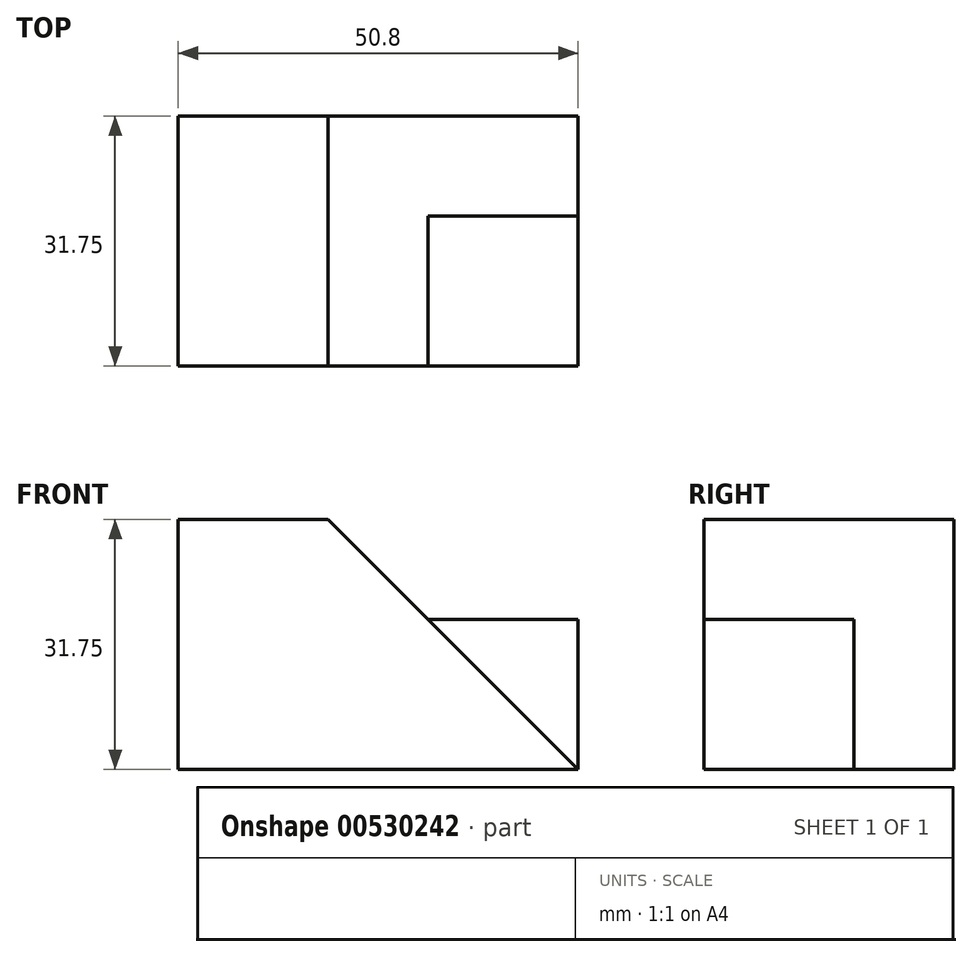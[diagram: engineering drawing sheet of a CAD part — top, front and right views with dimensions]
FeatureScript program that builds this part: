
annotation { "Feature Type Name" : "Feature", "Feature Type Description" : "" }
export const myFeature = defineFeature(function(context is Context, id is Id, definition is map)
    precondition{}
    {
        {
            var Q0;
            Q0=qCreatedBy(makeId("Front.planeOp"),FACE);
            var sketch = newSketch(context, id + "F0", { "sketchPlane" : qUnion([Q0])});
            skLineSegment(sketch, "E0", {"start": v(-59.12, 0) * mm, "end": v(-59.12, 31.75) * mm});
            skLineSegment(sketch, "E1", {"start": v(-59.12, 31.75) * mm, "end": v(-40.07, 31.75) * mm});
            skLineSegment(sketch, "E2", {"start": v(-40.07, 31.75) * mm, "end": v(-8.32, 0) * mm});
            skLineSegment(sketch, "E3", {"start": v(-8.32, 0) * mm, "end": v(-59.12, 0) * mm});
            skSolve(sketch);
        }
        {
            var Q0;
            Q0=makeQuery(id+"F0.imprint","IMPRINT",FACE,{"disambiguationData":[TD([[makeQuery(id+"F0.imprint","IMPRINT",EDGE,{"derivedFrom":sQuery(id+"F0.wireOp",EDGE,"E0")}),-1.0]])]});
            extrude(context, id + "F1", {"entities" : qUnion([Q0]), "depth" : 31.75 * mm, "offsetDistance" : 25.4 * mm});
        }
        {
            var Q0;
            Q0=makeQuery(id+"F1.opExtrude","CAP_FACE",FACE,{"disambiguationData":[OSD([sQuery(id+"F0.wireOp",EDGE,"E0"),sQuery(id+"F0.wireOp",EDGE,"E1"),sQuery(id+"F0.wireOp",EDGE,"E2"),sQuery(id+"F0.wireOp",EDGE,"E3")])],"isStart":false});
            var sketch = newSketch(context, id + "F2", { "sketchPlane" : qUnion([Q0])});
            skLineSegment(sketch, "E4", {"start": v(-27.37, 19.05) * mm, "end": v(-8.32, 19.05) * mm});
            skLineSegment(sketch, "E5", {"start": v(-8.32, 19.05) * mm, "end": v(-8.32, 0) * mm});
            skSolve(sketch);
        }
        {
            var Q0;
            Q0 = qSketchRegion(id + "F2", true);
            var Q1;
            {var subQ0=sQuery(id+"F2.wireOp",EDGE,"E4");Q1=makeQuery(id+"F2.imprint","IMPRINT",FACE,{"disambiguationData":[TD([[makeQuery(id+"F2.imprint","IMPRINT",EDGE,{"derivedFrom":subQ0}),-1.0]])]});}
            extrude(context, id + "F3", {"entities" : qUnion([Q0, Q1]), "oppositeDirection" : true, "depth" : 19.05 * mm, "offsetDistance" : 25.4 * mm});
        }
    });
